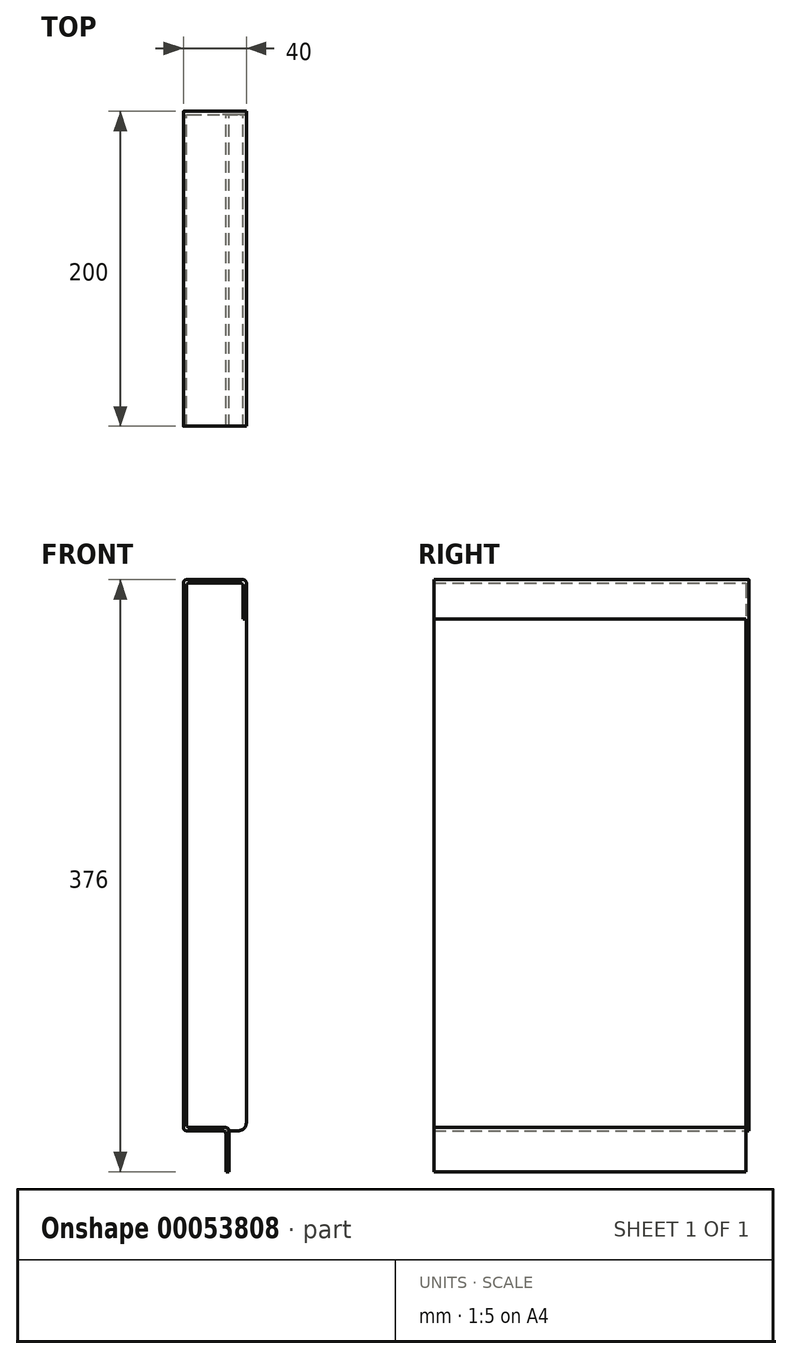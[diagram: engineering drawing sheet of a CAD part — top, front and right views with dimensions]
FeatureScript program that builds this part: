
annotation { "Feature Type Name" : "Feature", "Feature Type Description" : "" }
export const myFeature = defineFeature(function(context is Context, id is Id, definition is map)
    precondition{}
    {
        {
            var Q0;
            Q0=qCreatedBy(makeId("Front.planeOp"),FACE);
            var sketch = newSketch(context, id + "F0", { "sketchPlane" : qUnion([Q0])});
            skLineSegment(sketch, "E0", {"start": v(0, 0) * mm, "end": v(0, -350) * mm});
            skLineSegment(sketch, "E1", {"start": v(0, -350) * mm, "end": v(27, -350) * mm});
            skLineSegment(sketch, "E2", {"start": v(27, -350) * mm, "end": v(27, -376) * mm});
            skLineSegment(sketch, "E3", {"start": v(0, 0) * mm, "end": v(40, 0) * mm});
            skLineSegment(sketch, "E4", {"start": v(40, 0) * mm, "end": v(40, -25) * mm});
            skLineSegment(sketch, "E5.0", {"start": v(38, -2) * mm, "end": v(38, -25) * mm});
            skLineSegment(sketch, "E5.1", {"start": v(29, -348) * mm, "end": v(29, -376) * mm});
            skLineSegment(sketch, "E5.2", {"start": v(2, -348) * mm, "end": v(29, -348) * mm});
            skLineSegment(sketch, "E5.3", {"start": v(2, -2) * mm, "end": v(2, -348) * mm});
            skLineSegment(sketch, "E5.4", {"start": v(2, -2) * mm, "end": v(38, -2) * mm});
            skLineSegment(sketch, "E6", {"start": v(38, -25) * mm, "end": v(40, -25) * mm});
            skLineSegment(sketch, "E7", {"start": v(27, -376) * mm, "end": v(29, -376) * mm});
            skSolve(sketch);
        }
        {
            var Q0;
            Q0=qCreatedBy(makeId("Top.planeOp"),FACE);
            var sketch = newSketch(context, id + "F1", { "sketchPlane" : qUnion([Q0])});
            skLineSegment(sketch, "E8", {"start": v(0, 0) * mm, "end": v(0, 198) * mm});
            skSolve(sketch);
        }
        {
            var Q0;
            Q0=qSketchRegion(id+"F0",true);
            var Q1;
            Q1=qConstructionFilter(qBodyType(qCreatedBy(id+"F1",EDGE),BodyType.WIRE),ConstructionObject.NO);
            sweep(context, id + "F2", {"profiles" : qUnion([Q0]), "path" : qUnion([Q1])});
        }
        {
            var Q0;
            Q0=makeQuery(id+"F2.opSweep","CAP_FACE",FACE,{"disambiguationData":[OSD([sQuery(id+"F0.wireOp",EDGE,"E0"),sQuery(id+"F0.wireOp",EDGE,"E1"),sQuery(id+"F0.wireOp",EDGE,"E2"),sQuery(id+"F0.wireOp",EDGE,"E3"),sQuery(id+"F0.wireOp",EDGE,"E4"),sQuery(id+"F0.wireOp",EDGE,"E5.0"),sQuery(id+"F0.wireOp",EDGE,"E5.1"),sQuery(id+"F0.wireOp",EDGE,"E5.2"),sQuery(id+"F0.wireOp",EDGE,"E5.3"),sQuery(id+"F0.wireOp",EDGE,"E5.4"),sQuery(id+"F0.wireOp",EDGE,"E6"),sQuery(id+"F0.wireOp",EDGE,"E7"),sQuery(id+"F1.wireOp",VERTEX,"E8.end")])],"isStart":false});
            var sketch = newSketch(context, id + "F3", { "sketchPlane" : qUnion([Q0])});
            skLineSegment(sketch, "E9.0", {"start": v(0, -350) * mm, "end": v(0, 0) * mm});
            skLineSegment(sketch, "E10.0", {"start": v(-40, 0) * mm, "end": v(0, 0) * mm});
            skLineSegment(sketch, "E11.0", {"start": v(-40, -25) * mm, "end": v(-40, 0) * mm});
            skLineSegment(sketch, "E12.0", {"start": v(-40, -25) * mm, "end": v(-40, -345) * mm});
            skArc(sketch, "E13.0", {"start": v(-35, -350) * mm, "mid": v(-38.54, -348.54) * mm, "end": v(-40, -345) * mm});
            skLineSegment(sketch, "E14.0", {"start": v(-35, -350) * mm, "end": v(-29, -350) * mm});
            skLineSegment(sketch, "E15.0", {"start": v(-27, -350) * mm, "end": v(0, -350) * mm});
            skLineSegment(sketch, "E16", {"start": v(-29, -350) * mm, "end": v(-27, -350) * mm});
            skSolve(sketch);
        }
        {
            var Q0;
            Q0 = qSketchRegion(id + "F3", true);
            extrude(context, id + "F4", {"entities" : qUnion([Q0]), "operationType" : NewBodyOperationType.ADD, "depth" : 2 * mm});
        }
        {
            var Q0;
            Q0=makeQuery(id+"F4.boolean.opBoolean","MERGE",EDGE,{"derivedFrom":[makeQuery(id+"F2.opSweep","SWEPT_EDGE",EDGE,{"disambiguationData":[OSD([sQuery(id+"F0.wireOp",EDGE,"E0"),sQuery(id+"F0.wireOp",EDGE,"E3"),sQuery(id+"F1.wireOp",EDGE,"E8")])]}),makeQuery(id+"F4.opExtrude","SWEPT_EDGE",EDGE,{"disambiguationData":[OSD([sQuery(id+"F3.wireOp",EDGE,"E9.0"),sQuery(id+"F3.wireOp",EDGE,"E10.0")])]})]});
            var Q1;
            Q1=makeQuery(id+"F4.boolean.opBoolean","MERGE",EDGE,{"derivedFrom":[makeQuery(id+"F2.opSweep","SWEPT_EDGE",EDGE,{"disambiguationData":[OSD([sQuery(id+"F0.wireOp",EDGE,"E3"),sQuery(id+"F0.wireOp",EDGE,"E4"),sQuery(id+"F1.wireOp",EDGE,"E8")])]}),makeQuery(id+"F4.opExtrude","SWEPT_EDGE",EDGE,{"disambiguationData":[OSD([sQuery(id+"F3.wireOp",EDGE,"E10.0"),sQuery(id+"F3.wireOp",EDGE,"E11.0")])]})]});
            var Q2;
            Q2=makeQuery(id+"F2.opSweep","SWEPT_EDGE",EDGE,{"disambiguationData":[OSD([sQuery(id+"F0.wireOp",EDGE,"E5.2"),sQuery(id+"F0.wireOp",EDGE,"E5.3"),sQuery(id+"F1.wireOp",EDGE,"E8")])]});
            var Q3;
            Q3=makeQuery(id+"F2.opSweep","SWEPT_EDGE",EDGE,{"disambiguationData":[OSD([sQuery(id+"F0.wireOp",EDGE,"E5.1"),sQuery(id+"F0.wireOp",EDGE,"E5.2"),sQuery(id+"F1.wireOp",EDGE,"E8")])]});
            var Q4;
            Q4=makeQuery(id+"F2.opSweep","SWEPT_EDGE",EDGE,{"disambiguationData":[OSD([sQuery(id+"F0.wireOp",EDGE,"E5.3"),sQuery(id+"F0.wireOp",EDGE,"E5.4"),sQuery(id+"F1.wireOp",EDGE,"E8")])]});
            var Q5;
            Q5=makeQuery(id+"F4.boolean.opBoolean","MERGE",EDGE,{"derivedFrom":[makeQuery(id+"F2.opSweep","SWEPT_EDGE",EDGE,{"disambiguationData":[OSD([sQuery(id+"F0.wireOp",EDGE,"E0"),sQuery(id+"F0.wireOp",EDGE,"E1"),sQuery(id+"F1.wireOp",EDGE,"E8")])]}),makeQuery(id+"F4.opExtrude","SWEPT_EDGE",EDGE,{"disambiguationData":[OSD([sQuery(id+"F3.wireOp",EDGE,"E9.0"),sQuery(id+"F3.wireOp",EDGE,"E15.0")])]})]});
            var Q6;
            Q6=makeQuery(id+"F2.opSweep","SWEPT_EDGE",EDGE,{"disambiguationData":[OSD([sQuery(id+"F0.wireOp",EDGE,"E1"),sQuery(id+"F0.wireOp",EDGE,"E2"),sQuery(id+"F1.wireOp",EDGE,"E8")])]});
            var Q7;
            Q7=makeQuery(id+"F2.opSweep","SWEPT_EDGE",EDGE,{"disambiguationData":[OSD([sQuery(id+"F0.wireOp",EDGE,"E5.0"),sQuery(id+"F0.wireOp",EDGE,"E5.4"),sQuery(id+"F1.wireOp",EDGE,"E8")])]});
            fillet(context, id + "F5", {"entities" : qUnion([Q0, Q1, Q2, Q3, Q4, Q5, Q6, Q7]), "radius" : 2 * mm, "tangentPropagation" : true, "allowEdgeOverflow" : false});
        }
    });
